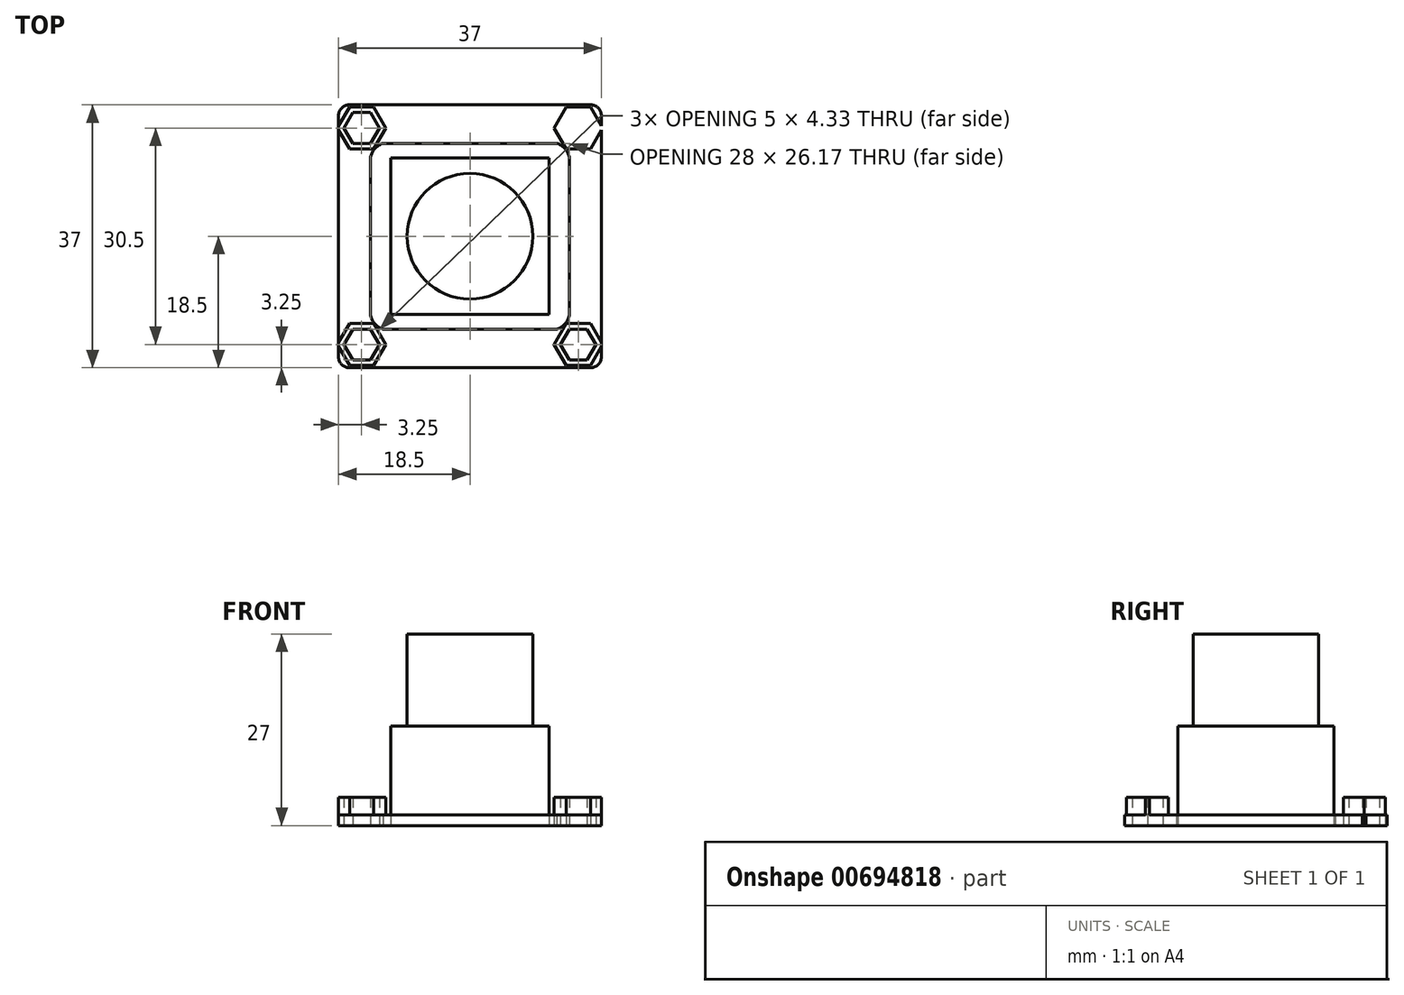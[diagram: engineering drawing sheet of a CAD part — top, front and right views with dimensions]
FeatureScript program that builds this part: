
annotation { "Feature Type Name" : "Feature", "Feature Type Description" : "" }
export const myFeature = defineFeature(function(context is Context, id is Id, definition is map)
    precondition{}
    {
        {
            var Q0;
            Q0=qCreatedBy(makeId("Top.planeOp"),FACE);
            var sketch = newSketch(context, id + "F0", { "sketchPlane" : qUnion([Q0])});
            skLineSegment(sketch, "E0.bottom", {"start": v(-15.25, 15.25) * mm, "end": v(15.25, 15.25) * mm, "construction": true});
            skLineSegment(sketch, "E0.top", {"start": v(-15.25, -15.25) * mm, "end": v(15.25, -15.25) * mm, "construction": true});
            skLineSegment(sketch, "E0.left", {"start": v(-15.25, 15.25) * mm, "end": v(-15.25, -15.25) * mm, "construction": true});
            skLineSegment(sketch, "E0.right", {"start": v(15.25, 15.25) * mm, "end": v(15.25, -15.25) * mm, "construction": true});
            skPoint(sketch, "E0.middle", {"position": v(0, 0) * mm});
            skLineSegment(sketch, "E1.bottom", {"start": v(-17, 18.5) * mm, "end": v(17, 18.5) * mm});
            skLineSegment(sketch, "E1.top", {"start": v(-17, -18.5) * mm, "end": v(17, -18.5) * mm});
            skLineSegment(sketch, "E1.left", {"start": v(-18.5, 17) * mm, "end": v(-18.5, -17) * mm});
            skLineSegment(sketch, "E1.right", {"start": v(18.5, 17) * mm, "end": v(18.5, -17) * mm});
            skPoint(sketch, "E2.visualSharp", {"position": v(-18.5, 18.5) * mm});
            skArc(sketch, "E2.filletArc", {"start": v(-17, 18.5) * mm, "mid": v(-18.06, 18.06) * mm, "end": v(-18.5, 17) * mm});
            skPoint(sketch, "E3.visualSharp", {"position": v(18.5, 18.5) * mm});
            skArc(sketch, "E3.filletArc", {"start": v(18.5, 17) * mm, "mid": v(18.06, 18.06) * mm, "end": v(17, 18.5) * mm});
            skPoint(sketch, "E4.visualSharp", {"position": v(18.5, -18.5) * mm});
            skArc(sketch, "E4.filletArc", {"start": v(17, -18.5) * mm, "mid": v(18.06, -18.06) * mm, "end": v(18.5, -17) * mm});
            skPoint(sketch, "E5.visualSharp", {"position": v(-18.5, -18.5) * mm});
            skArc(sketch, "E5.filletArc", {"start": v(-18.5, -17) * mm, "mid": v(-18.06, -18.06) * mm, "end": v(-17, -18.5) * mm});
            skCircle(sketch, "E6", {"center": v(-15.25, 15.25) * mm, "radius": 1.5 * mm, "construction": true});
            skCircle(sketch, "E7", {"center": v(15.25, 15.25) * mm, "radius": 1.5 * mm, "construction": true});
            skCircle(sketch, "E8", {"center": v(15.25, -15.25) * mm, "radius": 1.5 * mm, "construction": true});
            skCircle(sketch, "E9", {"center": v(-15.25, -15.25) * mm, "radius": 1.5 * mm, "construction": true});
            skCircle(sketch, "E10.cCircle", {"center": v(-15.25, 15.25) * mm, "radius": 2.5 * mm, "construction": true});
            skLineSegment(sketch, "E10.0", {"start": v(-12.75, 15.25) * mm, "end": v(-14, 13.08) * mm});
            skLineSegment(sketch, "E10.1", {"start": v(-14, 13.08) * mm, "end": v(-16.5, 13.08) * mm});
            skLineSegment(sketch, "E10.2", {"start": v(-16.5, 13.08) * mm, "end": v(-17.75, 15.25) * mm});
            skLineSegment(sketch, "E10.3", {"start": v(-17.75, 15.25) * mm, "end": v(-16.5, 17.42) * mm});
            skLineSegment(sketch, "E10.4", {"start": v(-16.5, 17.42) * mm, "end": v(-14, 17.42) * mm});
            skLineSegment(sketch, "E10.5", {"start": v(-14, 17.42) * mm, "end": v(-12.75, 15.25) * mm});
            skLineSegment(sketch, "E11", {"start": v(-5.45, 0) * mm, "end": v(0, 0) * mm, "construction": true});
            skLineSegment(sketch, "E12", {"start": v(0, 0) * mm, "end": v(0, 6) * mm});
            skLineSegment(sketch, "E13.MirrorCS", {"start": v(16.5, 17.42) * mm, "end": v(14, 17.42) * mm});
            skLineSegment(sketch, "E14.MirrorCS", {"start": v(14, 17.42) * mm, "end": v(12.75, 15.25) * mm});
            skLineSegment(sketch, "E15.MirrorCS", {"start": v(12.75, 15.25) * mm, "end": v(14, 13.08) * mm});
            skLineSegment(sketch, "E16.MirrorCS", {"start": v(14, 13.08) * mm, "end": v(16.5, 13.08) * mm});
            skLineSegment(sketch, "E17.MirrorCS", {"start": v(16.5, 13.08) * mm, "end": v(17.75, 15.25) * mm});
            skLineSegment(sketch, "E18.MirrorCS", {"start": v(17.75, 15.25) * mm, "end": v(16.5, 17.42) * mm});
            skLineSegment(sketch, "E19.MirrorCS", {"start": v(-17.75, -15.25) * mm, "end": v(-16.5, -17.42) * mm});
            skLineSegment(sketch, "E20.MirrorCS", {"start": v(-16.5, -17.42) * mm, "end": v(-14, -17.42) * mm});
            skLineSegment(sketch, "E21.MirrorCS", {"start": v(-14, -17.42) * mm, "end": v(-12.75, -15.25) * mm});
            skLineSegment(sketch, "E22.MirrorCS", {"start": v(-12.75, -15.25) * mm, "end": v(-14, -13.08) * mm});
            skLineSegment(sketch, "E23.MirrorCS", {"start": v(-14, -13.08) * mm, "end": v(-16.5, -13.08) * mm});
            skLineSegment(sketch, "E24.MirrorCS", {"start": v(-16.5, -13.08) * mm, "end": v(-17.75, -15.25) * mm});
            skLineSegment(sketch, "E25.MirrorCS", {"start": v(14, -17.42) * mm, "end": v(12.75, -15.25) * mm});
            skLineSegment(sketch, "E26.MirrorCS", {"start": v(16.5, -17.42) * mm, "end": v(14, -17.42) * mm});
            skLineSegment(sketch, "E27.MirrorCS", {"start": v(17.75, -15.25) * mm, "end": v(16.5, -17.42) * mm});
            skLineSegment(sketch, "E28.MirrorCS", {"start": v(16.5, -13.08) * mm, "end": v(17.75, -15.25) * mm});
            skLineSegment(sketch, "E29.MirrorCS", {"start": v(14, -13.08) * mm, "end": v(16.5, -13.08) * mm});
            skLineSegment(sketch, "E30.MirrorCS", {"start": v(12.75, -15.25) * mm, "end": v(14, -13.08) * mm});
            skLineSegment(sketch, "E31", {"start": v(14, 11.16) * mm, "end": v(14, -11.16) * mm});
            skLineSegment(sketch, "E32", {"start": v(-12.2, 13.08) * mm, "end": v(12.2, 13.08) * mm});
            skLineSegment(sketch, "E33", {"start": v(-14, 11.16) * mm, "end": v(-14, -11.16) * mm});
            skLineSegment(sketch, "E34", {"start": v(-12.2, -13.08) * mm, "end": v(12.2, -13.08) * mm});
            skArc(sketch, "E35", {"start": v(-12.2, 13.08) * mm, "mid": v(-13.36, 12.37) * mm, "end": v(-14, 11.16) * mm});
            skArc(sketch, "E36.MirrorCS", {"start": v(12.2, 13.08) * mm, "mid": v(13.36, 12.37) * mm, "end": v(14, 11.16) * mm});
            skArc(sketch, "E37.MirrorCS", {"start": v(-12.2, -13.08) * mm, "mid": v(-13.36, -12.37) * mm, "end": v(-14, -11.16) * mm});
            skArc(sketch, "E38.MirrorCS", {"start": v(12.2, -13.08) * mm, "mid": v(13.36, -12.37) * mm, "end": v(14, -11.16) * mm});
            skCircle(sketch, "E39.cCircle", {"center": v(-15.25, 15.25) * mm, "radius": 3.4 * mm, "construction": true});
            skLineSegment(sketch, "E39.0", {"start": v(-11.84, 15.25) * mm, "end": v(-13.55, 12.3) * mm});
            skLineSegment(sketch, "E39.1", {"start": v(-13.55, 12.3) * mm, "end": v(-16.95, 12.3) * mm});
            skLineSegment(sketch, "E39.2", {"start": v(-16.95, 12.3) * mm, "end": v(-18.66, 15.25) * mm});
            skLineSegment(sketch, "E39.3", {"start": v(-18.66, 15.25) * mm, "end": v(-16.95, 18.2) * mm});
            skLineSegment(sketch, "E39.4", {"start": v(-16.95, 18.2) * mm, "end": v(-13.55, 18.2) * mm});
            skLineSegment(sketch, "E39.5", {"start": v(-13.55, 18.2) * mm, "end": v(-11.84, 15.25) * mm});
            skArc(sketch, "E40.MirrorCS", {"start": v(17, 18.5) * mm, "mid": v(18.06, 18.06) * mm, "end": v(18.5, 17) * mm});
            skLineSegment(sketch, "E41.MirrorCS", {"start": v(13.55, 18.2) * mm, "end": v(11.84, 15.25) * mm});
            skLineSegment(sketch, "E42.MirrorCS", {"start": v(13.55, 12.3) * mm, "end": v(16.95, 12.3) * mm});
            skLineSegment(sketch, "E43.MirrorCS", {"start": v(11.84, 15.25) * mm, "end": v(13.55, 12.3) * mm});
            skLineSegment(sketch, "E44.MirrorCS", {"start": v(18.66, 15.25) * mm, "end": v(16.95, 18.2) * mm});
            skCircle(sketch, "E45.MirrorC", {"center": v(15.25, 15.25) * mm, "radius": 2.5 * mm, "construction": true});
            skLineSegment(sketch, "E46.MirrorCS", {"start": v(16.95, 18.2) * mm, "end": v(13.55, 18.2) * mm});
            skCircle(sketch, "E47.MirrorC", {"center": v(15.25, 15.25) * mm, "radius": 3.4 * mm, "construction": true});
            skLineSegment(sketch, "E48.MirrorCS", {"start": v(16.95, 12.3) * mm, "end": v(18.66, 15.25) * mm});
            skArc(sketch, "E49.MirrorCS", {"start": v(18.5, -17) * mm, "mid": v(18.06, -18.06) * mm, "end": v(17, -18.5) * mm});
            skArc(sketch, "E50.MirrorCS", {"start": v(-17, -18.5) * mm, "mid": v(-18.06, -18.06) * mm, "end": v(-18.5, -17) * mm});
            skLineSegment(sketch, "E51.MirrorCS", {"start": v(-16.95, -18.2) * mm, "end": v(-13.55, -18.2) * mm});
            skLineSegment(sketch, "E52.MirrorCS", {"start": v(16.95, -18.2) * mm, "end": v(13.55, -18.2) * mm});
            skCircle(sketch, "E53.MirrorC", {"center": v(-15.25, -15.25) * mm, "radius": 3.4 * mm, "construction": true});
            skLineSegment(sketch, "E54.MirrorCS", {"start": v(18.66, -15.25) * mm, "end": v(16.95, -18.2) * mm});
            skCircle(sketch, "E55.MirrorC", {"center": v(-15.25, -15.25) * mm, "radius": 2.5 * mm, "construction": true});
            skLineSegment(sketch, "E56.MirrorCS", {"start": v(16.95, -12.3) * mm, "end": v(18.66, -15.25) * mm});
            skLineSegment(sketch, "E57.MirrorCS", {"start": v(-11.84, -15.25) * mm, "end": v(-13.55, -12.3) * mm});
            skCircle(sketch, "E58.MirrorC", {"center": v(15.25, -15.25) * mm, "radius": 2.5 * mm, "construction": true});
            skLineSegment(sketch, "E59.MirrorCS", {"start": v(13.55, -12.3) * mm, "end": v(16.95, -12.3) * mm});
            skLineSegment(sketch, "E60.MirrorCS", {"start": v(13.55, -18.2) * mm, "end": v(11.84, -15.25) * mm});
            skLineSegment(sketch, "E61.MirrorCS", {"start": v(-13.55, -12.3) * mm, "end": v(-16.95, -12.3) * mm});
            skLineSegment(sketch, "E62.MirrorCS", {"start": v(11.84, -15.25) * mm, "end": v(13.55, -12.3) * mm});
            skLineSegment(sketch, "E63.MirrorCS", {"start": v(-16.95, -12.3) * mm, "end": v(-18.66, -15.25) * mm});
            skCircle(sketch, "E64.MirrorC", {"center": v(15.25, -15.25) * mm, "radius": 3.4 * mm, "construction": true});
            skLineSegment(sketch, "E65.MirrorCS", {"start": v(-13.55, -18.2) * mm, "end": v(-11.84, -15.25) * mm});
            skLineSegment(sketch, "E66.MirrorCS", {"start": v(-18.66, -15.25) * mm, "end": v(-16.95, -18.2) * mm});
            skSolve(sketch);
        }
        {
            var Q0;
            Q0=makeQuery(id+"F0.imprint","IMPRINT",FACE,{"disambiguationData":[TD([[makeQuery(id+"F0.imprint","IMPRINT",EDGE,{"derivedFrom":sQuery(id+"F0.wireOp",EDGE,"E1.bottom")}),-1.0]])]});
            extrude(context, id + "F1", {"entities" : qUnion([Q0]), "depth" : 1.5 * mm, "offsetDistance" : 25 * mm});
        }
        {
            var Q0;
            Q0=makeQuery(id+"F0.imprint","IMPRINT",FACE,{"disambiguationData":[TD([[makeQuery(id+"F0.imprint","IMPRINT",EDGE,{"derivedFrom":sQuery(id+"F0.wireOp",EDGE,"E10.0")}),1.0]])]});
            var Q1;
            {var subQ5=sQuery(id+"F0.wireOp",EDGE,"E52.MirrorCS");Q1=makeQuery(id+"F0.imprint","IMPRINT",FACE,{"disambiguationData":[TD([[makeQuery(id+"F0.imprint","IMPRINT",EDGE,{"derivedFrom":subQ5}),-1.0]])]});}
            var Q2;
            Q2=makeQuery(id+"F0.imprint","IMPRINT",FACE,{"disambiguationData":[TD([[makeQuery(id+"F0.imprint","IMPRINT",EDGE,{"derivedFrom":sQuery(id+"F0.wireOp",EDGE,"E24.MirrorCS")}),-1.0]])]});
            var Q3;
            Q3=makeQuery(id+"F0.imprint","IMPRINT",FACE,{"disambiguationData":[TD([[makeQuery(id+"F0.imprint","IMPRINT",EDGE,{"derivedFrom":sQuery(id+"F0.wireOp",EDGE,"E16.MirrorCS")}),-1.0]])]});
            extrude(context, id + "F2", {"entities" : qUnion([Q0, Q1, Q2, Q3]), "operationType" : NewBodyOperationType.ADD, "depth" : 4 * mm, "offsetDistance" : 25 * mm});
        }
        {
            var Q0;
            Q0=qCreatedBy(makeId("Top.planeOp"),FACE);
            var sketch = newSketch(context, id + "F3", { "sketchPlane" : qUnion([Q0])});
            skLineSegment(sketch, "E67.bottom", {"start": v(-11.15, 11) * mm, "end": v(11.15, 11) * mm});
            skLineSegment(sketch, "E67.top", {"start": v(-11.15, -11) * mm, "end": v(11.15, -11) * mm});
            skLineSegment(sketch, "E67.left", {"start": v(-11.15, 11) * mm, "end": v(-11.15, -11) * mm});
            skLineSegment(sketch, "E67.right", {"start": v(11.15, 11) * mm, "end": v(11.15, -11) * mm});
            skPoint(sketch, "E67.middle", {"position": v(0, 0) * mm});
            skCircle(sketch, "E68", {"center": v(0, 0) * mm, "radius": 8.84 * mm});
            skSolve(sketch);
        }
        {
            var Q0;
            Q0=makeQuery(id+"F3.imprint","IMPRINT",FACE,{"disambiguationData":[TD([[makeQuery(id+"F3.imprint","IMPRINT",EDGE,{"derivedFrom":sQuery(id+"F3.wireOp",EDGE,"E67.bottom")}),-1.0]])]});
            extrude(context, id + "F4", {"entities" : qUnion([Q0]), "depth" : 14 * mm, "offsetDistance" : 25 * mm});
        }
        {
            var Q0;
            Q0=makeQuery(id+"F3.imprint","IMPRINT",FACE,{"disambiguationData":[TD([[makeQuery(id+"F3.imprint","IMPRINT",EDGE,{"derivedFrom":sQuery(id+"F3.wireOp",EDGE,"E68")}),1.0]])]});
            extrude(context, id + "F5", {"entities" : qUnion([Q0]), "operationType" : NewBodyOperationType.ADD, "depth" : 27 * mm, "offsetDistance" : 25 * mm});
        }
    });
